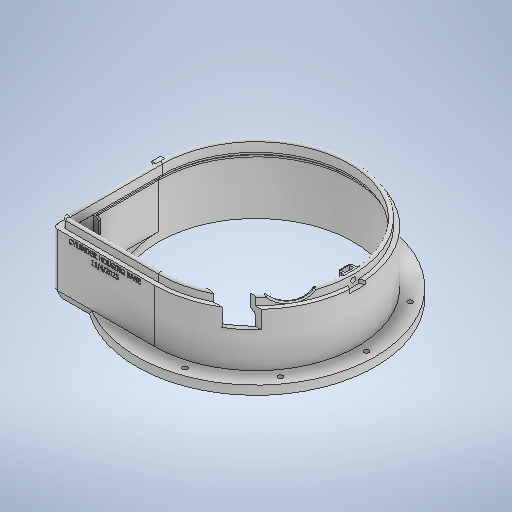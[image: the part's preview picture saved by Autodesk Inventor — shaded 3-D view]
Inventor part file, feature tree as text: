
AUTODESK INVENTOR PART (.ipt)
format: ipt  version: 2025 (Build 290162000, 162)  size: 1,288,704 bytes
history: native  units: mm
features: sketch x18, extrude x13, fillet x7, chamfer x5, hole x2, pattern_circular x1, other x1, plane x1, emboss x1
ambient origin geometry x8: Origin, YZ Plane, XZ Plane, XY Plane, X Axis, Y Axis, Z Axis, Center Point
bodies: Solid1 (feature_tree)
feature tree (49):
  extrude  "Base"  Depth=220.0mm
  hole  "Cylinder Mount Holes"  [1 undecoded]
  pattern_circular  "Circular Pattern1"  Count=10 Angle=360.0deg
  extrude  "Walls"  Depth=220.0mm
  extrude  "Corner Fill"  Depth=30.0mm TaperAngle=0.0deg
  fillet  "Corner Fillet"  Radius=5.0mm
  other  "Seal Groove"
  extrude  "Overhang for Lip"  Depth=3.0mm
  extrude  "Lip"  Depth=4.0mm
  chamfer  "Overhang Chamfer"  Distance=4.0mm
  fillet  "Overhang Fillet"  Radius=10.0mm
  extrude  "Nut Seat Body"  Depth=4.0mm
  chamfer  "Nut Seat Body Chamfer"  Distance=20.0mm
  extrude  "Nut Seat"  Depth=10.0mm
  extrude  "Front Alignment Tab"  Depth=1.0mm
  hole  "Bolt Holt"  [1 undecoded]
  extrude  "Hinge Tab"  Depth=4.0mm TaperAngle=0.0deg
  fillet  "Nut Seat Body Fillets"  Radius=7.5mm
  fillet  "Top Edge Fillet"  Radius=10.0mm
  sketch  "Sketch15"  dims[d49=12.7mm d50=0.0mm d59=6.0mm]
  extrude  "LV Window"  Depth=3.0mm
  fillet  "LV Window Fillet"  Radius=10.0mm
  plane  "Work Plane1"
  extrude  "8020 Ledge"  Depth=42.0mm
  extrude  "Ledge Walls"  Depth=22.0mm
  chamfer  "Ledge Chamfer"  [1 undecoded]
  fillet  "Ledge Fillets"  Radius=1.5mm
  chamfer  "Ledge Wall Chamfer"  [1 undecoded]
  extrude  "8020 Window"  Depth=10.0mm
  chamfer  "Chamfer5"  Distance=25.0mm
  fillet  "Fillet7"  Radius=88.16mm
  emboss  "Emboss1"
  sketch  "Sketch1"  dims[d0=270.0mm d1=220.0mm]
  sketch  "Sketch2"  dims[d2=10.0mm d3=0.0mm]
  sketch  "Sketch3"  dims[d4=5.5mm d5=6.0mm d6=4.0mm d7=2.0mm d8=90.0deg d9=8.0mm d10=20.594885mm d11=125.0mm d12=100.0mm d13=360.0deg]
  sketch  "Sketch4"  dims[d15=230.0mm d16=220.0mm]
  sketch  "Sketch6"  dims[d17=60.0mm d18=0.0mm d19=30.0mm d20=0.0mm d21=5.0mm]
  sketch  "Sketch7"  dims[d26=2.0mm d27=3.0mm]
  sketch  "Sketch8"  dims[d29=90.0deg d30=4.0mm d31=4.0mm d32=0.0mm d33=10.0mm d34=0.0mm]
  sketch  "Sketch9"  dims[d35=4.0mm d36=2.0mm d37=45.0deg d38=4.0mm]
  sketch  "Sketch10"  dims[d39=14.0mm]
  sketch  "Sketch12"  dims[d40=10.0mm d41=20.0mm d42=0.0mm]
  sketch  "Sketch13"  dims[d43=10.2mm d44=2.0mm d45=45.0deg d46=10.0mm]
  sketch  "Sketch14"  dims[d47=5.0mm d48=1.0mm]
  sketch  "Sketch16"  dims[d60=9.0mm d61=4.0mm d62=0.0mm]
  sketch  "Sketch18"  dims[d63=5.5mm d64=6.0mm d65=4.0mm d66=2.0mm d67=90.0deg d68=8.0mm d69=20.594885mm d70=7.5mm d71=10.0mm d72=0.0mm]
  sketch  "Sketch19"  dims[d73=1.0mm d74=3.0mm d75=10.0mm]
  sketch  "Sketch20"  dims[d76=2.0mm d77=42.0mm]
  sketch  "Sketch21"  dims[d78=53.266mm d79=22.0mm d80=0.0mm d81=0.0mm d82=1.5mm d85=-20.0mm d86=10.0mm d87=25.0mm d88=88.16mm d89=10.0mm d90=0.0mm d91=2.5mm d92=2.5mm d93=17.5mm d94=0.0mm d95=10.0mm d96=2.0mm d97=45.0deg d98=2.0mm d99=3.0mm d100=2.0mm d101=45.0deg d102=30.0mm d103=20.0mm d104=88.16mm d105=0.0mm d106=0.0mm d107=114.0mm d108=5.0mm d109=10.0mm d110=45.0deg d111=0.15mm d112=1.0mm d113=0.0mm]
note: 4 required parameter values undecoded (feature->parameter linkage not recoverable at this tier; creation-order binding heuristic only, values carry confidence <= 0.55)
